# Revit family: Electronics_Community-Point-Source_Biamp_Stage-Monitor_MX_8
name_source: partatom
category: Communication Devices
units: mm (PartAtom-declared; Revit-internal decimal feet)

## family parameters
Cut with Voids When Loaded = No
Host = Face
Maintain Annotation Orientation = No
OmniClass Number = 23.85.10.11.14.14.14
Part Type = Normal
Room Calculation Point = No
Round Connector Dimension = Use Diameter
Shared = No

## types (2) — shared parameters
Axial Q / DI = 5.7 / 7.6, 500 Hz to 6 kHz
Connector Description = NL4, Terminal strip; 150W continuous, 375W program 35 volts RMS, 77 volts momentary peak
Crossover Frequency = 1.3 kHz
Default Elevation = 4' - 0"
Depth = 1' - 2 1/2"
Description = MX8 M-Class Low Profile 8-Inch Two-Way Full-Range Coaxial Stage Monitor
Driver Protection = DYNA-TECH™ driver protection system
Drivers = LF (1) 8-inch cone, HF (1) 1.25-inch exit
Enclosure = 11-ply cross-laminated birch
Handles = (1) Ergo-Grip™ rear pocket handle
Height = 0' - 10 1/2"
Input Connection = (2) paralleled NL4-compatible locking connectors internally looped to one 2-terminal barrier strip
Loudspeaker Type = Two-way, full-range coaxial floor monitor
Manufacturer = Biamp
Maximum Output = 118 dB SPL / 125 dB SPL (peak)
Minimum Impedance = 5.7 ohms @ 230 Hz
Nominal Impedance = 8 ohms
Nominal –6dB Beamwidth = 115° H (+46º / -46º, 500 Hz to 6 kHz), 115° V (+46º / -46º, 500 Hz to 6 kHz)
Operating Range = 80 Hz to 18 kHz, 90 Hz to 16 kHz (±3 dB)
Optional Accessories = MX-Y8B mounting yoke bracket, black
Product Documentation Link = https://downloads.biamp.com
Product Page URL = https://www.biamp.com
Product data url = https://www.bimobject.com
Recommended Power Amplifier = 300W to 450W @ 8 ohms
Recommended Signal Processing = 90 Hz high pass filter
Required Accessories = 24 dB/Octave 100 Hz high pass filter
Sensitivity (1W/1m) = 96 dB SPL (125 Hz to 12.5 kHz 1/3 octave bands), 96 dB SPL (250 Hz to 4 kHz speech range)
URL = https://www.biamp.com
Weight = 17.00 lbf
Width = 0' - 11"

## per-type parameters (varying)
| type | Grill Material | Housing Material |
| MX8 B | Biamp - Plastic - Black(Grid) | Biamp - Plastic - Black |
| MX8 W | Biamp - Plastic - White(Grid) | Biamp - Plastic - White |

note: column(s) folded — value = type name in every type: Model

## geometry (parser evidence)
native form markers: Sweep x1
no freeform markers — native parametric forms only
